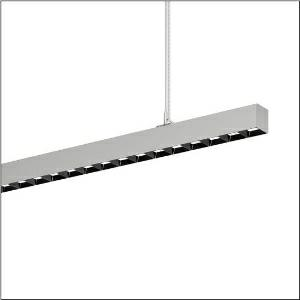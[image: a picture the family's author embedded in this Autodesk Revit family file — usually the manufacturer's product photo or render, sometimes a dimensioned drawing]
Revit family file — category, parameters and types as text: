
# Revit family: silica_r__21_51mx32tctds_853f
name_source: partatom
category: Lighting Fixtures
units: mm (PartAtom-declared; Revit-internal decimal feet)

## family parameters
Cut with Voids When Loaded = No
Host = Face
Light Source = No
Part Type = Normal
Room Calculation Point = No
Round Connector Dimension = Use Diameter
Shared = No

## types (1)
- --- (1 x LED, 15540 lm, 133.6 W, 6500K)
    Apparent Load = 134 VA
    CIE Flux Codes = 84 99 100 60 100
    Color Rendering = 80
    Color Temperature = 6500K
    Default Elevation = 1800 mm
    Description = Silica® 21, office luminaire, primary light control with darklight reflector, of PMMA, black, CAT 2 (L<= 3000cd/m²), light emission: direct/indirect distribution, primary light characteristic: symmetric, installation type: suspended mounting, LED, rated luminous flux: 15.540lm, luminous efficacy: 111lm/W, light colour: 8tw, colour temperature: 2700..6500K, control gear: DALI DT8, with terminal, 3+2-pole, max. 2.5mm², mains connection: 220..240V, AC, 50/60Hz, rated input power: 140.3W, luminaire housing, of aluminium, metallic grey (RAL 9006), length: 3.004mm, width: 53mm, height: 53mm, protection rating (complete): IP20, insulation class (complete): insulation class I (protective earthing), certification: CE, permissible operating ambient temperature: 0..+35°C, standard: EN 50419, packaging unit: 1 piece
    Height = 53 mm
    Lamp = 1 x LED
    Lamp Light Flux = 15540 lm
    Lamp Power = 133.6 W
    Lamp count = 1
    Length = 3004 mm
    Luminous efficacy = 116 lm/W
    Manufacturer = Siteco
    ModVariant = No
    Model = 51MX32TCTDS
    Mounting Place = Ceiling
    Mounting Type = Pendant
    Number of Poles = 1
    OnlyDefault = Yes
    Power Factor = 1
    Product Name = Silica® 21
    Product group = office luminaire | ceiling pendant
    ProductGroupID = 904
    Protection Class = Protection class I
    Protection Degree = IP 20
    RLX_Detail_Level = 1
    RLX_Emergency_Light_Flux = 0 lm
    RLX_Emergency_Type = 0
    RLX_Emergency_Type_DB = No
    RlxData = <blob elided: 63169 chars, md5=22075873>
    Socket = socket
    Standby Power = 0 W
    System Light Flux = 15540 lm
    System Power = 134 W
    Type Comments = individual setting
    Type Image = l_1335859.jpg
    URL = http://relux.com
    VarID = @adj_139914
    Voltage = 0 V
    Weight = 0.00 kg
    Width = 53 mm

## geometry (parser evidence)
native form markers: Blend x4, Sweep x14
no freeform markers — native parametric forms only
